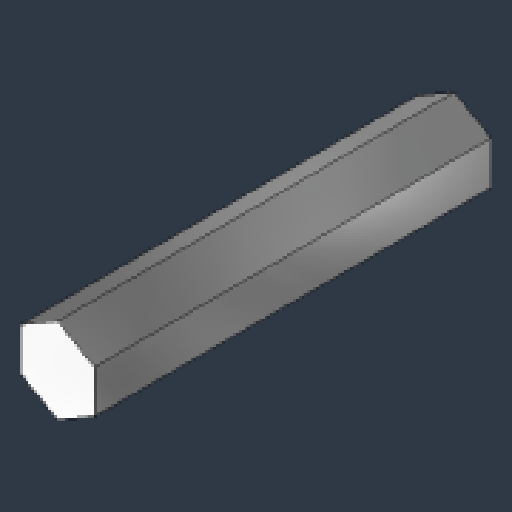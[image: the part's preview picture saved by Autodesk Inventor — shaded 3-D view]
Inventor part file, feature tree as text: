
AUTODESK INVENTOR PART (.ipt)
format: ipt  version: 2024.3 (Build 283343000, 343)  size: 94,720 bytes
history: native  units: in
note: dims shown in document units (in); Inventor stores cm internally (conversion verified against a paired STEP export)
features: extrude x1, sketch x1
ambient origin geometry x8: Origin, YZ Plane, XZ Plane, XY Plane, X Axis, Y Axis, Z Axis, Center Point
bodies: Solid1 (feature_tree)
feature tree (2):
  extrude  "Extrusion1"  Depth=2.7475in TaperAngle=0.0deg
  sketch  "Sketch1"  dims[d0=0.5in d1=2.7475in d2=0.0in]
